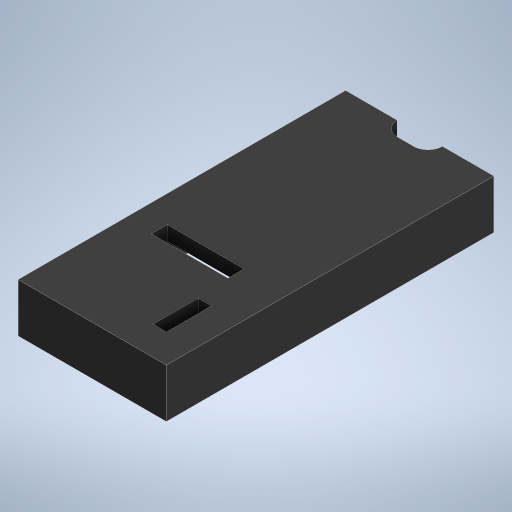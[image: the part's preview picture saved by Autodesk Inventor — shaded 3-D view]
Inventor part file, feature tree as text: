
AUTODESK INVENTOR PART (.ipt)
format: ipt  version: 2024 (Build 280153000, 153)  size: 274,432 bytes
history: native  units: in
note: dims shown in document units (in); Inventor stores cm internally (conversion verified against a paired STEP export)
features: extrude x4, sketch x4, fillet x1, projected_geometry x1
ambient origin geometry x8: Origin, YZ Plane, XZ Plane, XY Plane, X Axis, Y Axis, Z Axis, Center Point
bodies: Solid1 (feature_tree)
feature tree (10):
  extrude  "Extrusion1"  Depth=2.6in
  extrude  "Extrusion2"  Depth=0.125in
  extrude  "Extrusion3"  Depth=0.3in TaperAngle=0.0deg
  fillet  "Fillet1"  Radius=0.125in
  extrude  "Extrusion4"  Depth=0.3937in
  sketch  "Sketch1"  dims[d0=1.04in d1=2.6in]
  sketch  "Sketch2"  dims[d2=0.125in d3=0.1969in]
  sketch  "Sketch3"  dims[d4=0.1969in d5=0.3in d6=0.0in d8=0.125in]
  projected_geometry  "Projected Loop1"
  sketch  "Sketch4"  dims[d9=0.1181in d10=0.3937in d11=0.0197in d12=0.28in d13=0.125in d14=0.0in d15=0.125in d16=0.0in d17=0.125in d18=0.01in d19=0.125in d20=0.0in]
